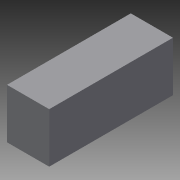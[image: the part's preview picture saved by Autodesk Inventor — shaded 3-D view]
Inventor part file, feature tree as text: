
AUTODESK INVENTOR PART (.ipt)
format: ipt  version: 2015 (Build 190159000, 159)  size: 68,608 bytes
history: native  units: mm
features: extrude x1, sketch x1
ambient origin geometry x8: Origin, YZ Plane, XZ Plane, XY Plane, X Axis, Y Axis, Z Axis, Center Point
bodies: Solid1 (feature_tree)
feature tree (2):
  extrude  "Extrusion1"  Depth=808.566667mm
  sketch  "Sketch1"  dims[d0=685.8mm d1=808.566667mm d2=2011.68mm d3=0.0mm]
